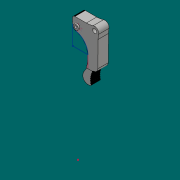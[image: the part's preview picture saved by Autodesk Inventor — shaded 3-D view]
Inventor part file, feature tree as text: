
AUTODESK INVENTOR PART (.ipt)
format: ipt  version: 2018 (Build 220112000, 112)  size: 2,591,232 bytes
history: native  units: mm
features: extrude x17, sketch x17, other x2, fillet x2, chamfer x2, projected_geometry x2
ambient origin geometry x8: Origin, YZ Plane, XZ Plane, XY Plane, X Axis, Y Axis, Z Axis, Center Point
bodies: Body1 (feature_tree)
feature tree (42):
  other  "ソリッド1"
  other  "メッシュ フィーチャ1"
  extrude  "押し出し1"  Depth=10.0mm TaperAngle=0.0deg
  extrude  "押し出し2"  Depth=2.0mm
  extrude  "押し出し3"  Depth=10.0mm TaperAngle=0.0deg
  extrude  "押し出し4"  Depth=10.0mm TaperAngle=0.0deg
  extrude  "押し出し5"  Depth=2.5mm
  extrude  "押し出し6"  Depth=4.0mm
  extrude  "押し出し7"  Depth=10.0mm TaperAngle=0.0deg
  fillet  "フィレット2"  Radius=4.1mm
  extrude  "押し出し8"  Depth=10.0mm TaperAngle=0.0deg
  extrude  "押し出し9"  Depth=8.0mm
  extrude  "押し出し10"  Depth=10.0mm TaperAngle=0.0deg
  extrude  "押し出し11"  Depth=7.9mm
  extrude  "押し出し12"  Depth=10.0mm TaperAngle=0.0deg
  extrude  "押し出し13"  Depth=20.0mm
  chamfer  "面取り1"  Distance=10.0mm
  chamfer  "面取り2"  Distance=10.0mm
  fillet  "フィレット3"  Radius=10.0mm
  extrude  "押し出し14"  Depth=1.9mm
  extrude  "押し出し15"  Depth=1.3mm
  extrude  "押し出し16"  Depth=10.0mm TaperAngle=0.0deg
  extrude  "押し出し17"  Depth=8.5mm
  sketch  "スケッチ1"
  sketch  "スケッチ2"
  sketch  "スケッチ3"
  sketch  "スケッチ4"
  sketch  "スケッチ5"
  sketch  "スケッチ6"
  sketch  "スケッチ7"
  sketch  "スケッチ8"
  sketch  "スケッチ9"
  sketch  "スケッチ10"
  sketch  "スケッチ11"
  sketch  "スケッチ12"
  sketch  "スケッチ13"
  sketch  "スケッチ15"
  projected_geometry  "投影ループ1"
  sketch  "スケッチ16"
  sketch  "スケッチ17"
  sketch  "スケッチ18"
  projected_geometry  "投影ループ2"
